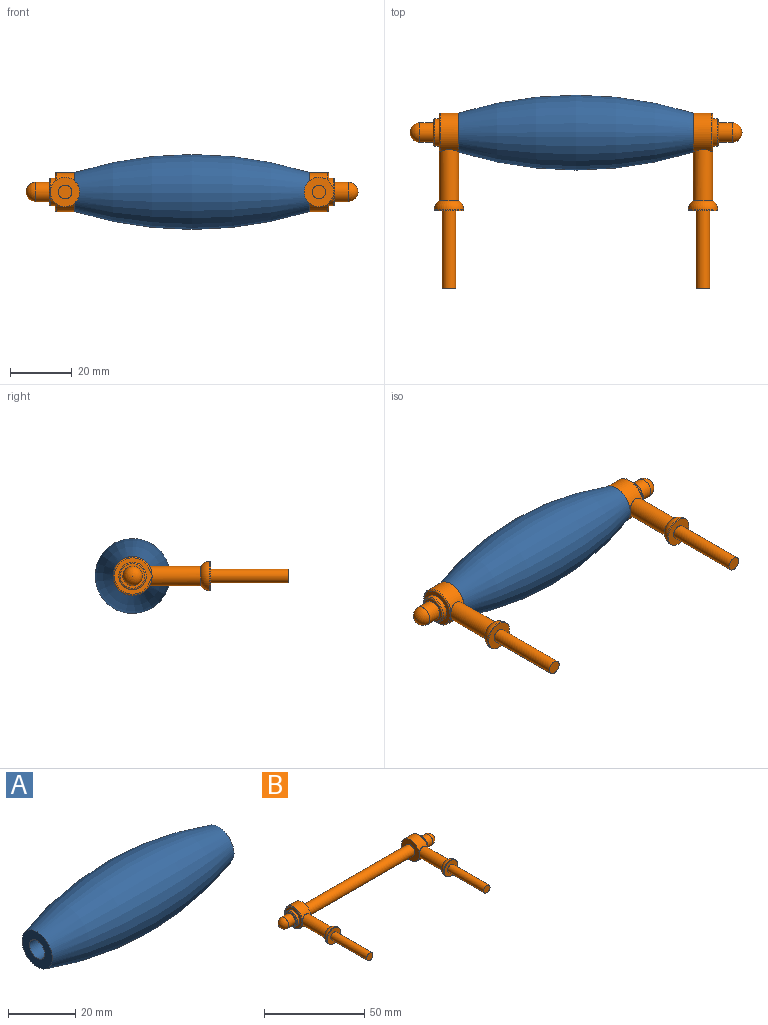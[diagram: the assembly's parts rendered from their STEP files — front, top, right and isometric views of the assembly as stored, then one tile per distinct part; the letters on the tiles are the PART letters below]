
ASSEMBLY  parts=2 mates=1
PART A: 4 faces, bbox 76.2x24.4x24.4 mm
  f0: cylinder r=3.17mm len=76.2mm, axis (-1,0,0), area 1520.1mm2, adj f1,f3
  f1: plane 12.7x12.7mm, normal (1,0,0), area 95mm2, adj f0,f2
  f2: revolved ~76.2x24.4mm, area 4981.2mm2, adj f1,f3
  f3: plane 12.7x12.7mm, normal (-1,0,0), area 95mm2, adj f0,f2
PART B: 35 faces, bbox 108x57.7x13.8 mm
  f0: cylinder r=3.17mm len=16.09mm, axis (0,1,0), area 318.8mm2, adj f2,f26,f28,f34
  f1: cylinder r=3.17mm len=16.09mm, axis (0,1,0), area 318.8mm2, adj f3,f29,f31,f33
  f2: cylinder r=6.35mm len=12.7mm, axis (-1,0,0), area 203.8mm2, adj f0,f7,f27
  f3: cylinder r=6.35mm len=12.7mm, axis (-1,0,0), area 203.8mm2, adj f1,f9,f30
  f4: plane 8x8mm, normal (1,0,0), area 18.6mm2, adj f16,f25
  f5: cylinder r=4.45mm len=8.89mm, axis (-1,0,0), area 40.8mm2, adj f6,f25
  f6: plane 12.26x11.81mm, normal (1,0,0), area 48mm2, adj f5,f26,f27,f28
  f7: plane 12.7x12.7mm, normal (-1,0,0), area 95mm2, adj f2,f8
  f8: cylinder r=3.17mm len=76.2mm, axis (-1,0,0), area 1520.1mm2, adj f7,f9
  f9: plane 12.7x12.7mm, normal (1,0,0), area 95mm2, adj f3,f8
  f10: plane 12.26x11.81mm, normal (-1,0,0), area 48mm2, adj f11,f29,f30,f31
  f11: cylinder r=4.45mm len=8.89mm, axis (-1,0,0), area 40.8mm2, adj f10,f32
  f12: plane 8x8mm, normal (-1,0,0), area 18.6mm2, adj f13,f32
  f13: cylinder r=3.17mm len=6.35mm, axis (-1,0,0), area 88.7mm2, adj f12,f14
  f14: sphere r=3.17mm, area 63.3mm2, adj f13
  f15: sphere r=3.17mm, area 63.3mm2, adj f16
  f16: cylinder r=3.17mm len=6.35mm, axis (-1,0,0), area 88.7mm2, adj f4,f15
  f17: cylinder r=4.76mm len=9.53mm, axis (0,-1,0), area 12.7mm2, adj f20,f33
  f18: plane 4.45x4.45mm, normal (0,-1,0), area 15.5mm2, adj f19
  f19: cylinder r=2.22mm len=25.4mm, axis (0,1,0), area 354.7mm2, adj f18,f20
  f20: plane 9.53x9.53mm, normal (0,-1,0), area 55.7mm2, adj f17,f19
  f21: cylinder r=4.76mm len=9.53mm, axis (0,-1,0), area 12.7mm2, adj f24,f34
  f22: plane 4.45x4.45mm, normal (0,-1,0), area 15.5mm2, adj f23
  f23: cylinder r=2.22mm len=25.4mm, axis (0,1,0), area 354.7mm2, adj f22,f24
  f24: plane 9.53x9.53mm, normal (0,-1,0), area 55.7mm2, adj f21,f23
  f25: torus R=4mm, axis (1,0,0), area 18.8mm2, adj f4,f5
  f26: bspline ~1.72x0.67mm, area 0.4mm2, adj f0,f6,f27
  f27: torus R=5.91mm, axis (1,0,0), area 24.9mm2, adj f2,f6,f26,f28
  f28: bspline ~1.84x0.69mm, area 0.4mm2, adj f0,f6,f27
  f29: bspline ~1.84x0.69mm, area 0.4mm2, adj f1,f10,f30
  f30: torus R=5.91mm, axis (1,0,0), area 24.9mm2, adj f3,f10,f29,f31
  f31: bspline ~1.72x0.67mm, area 0.4mm2, adj f1,f10,f30
  f32: torus R=4mm, axis (1,0,0), area 18.8mm2, adj f11,f12
  f33: torus R=1.59mm, axis (0,1,0), area 88mm2, adj f1,f17
  f34: torus R=1.59mm, axis (0,1,0), area 88mm2, adj f0,f21
PLACE A t=(21.78,20.34,11.64)mm
PLACE B t=(21.78,20.34,11.64)mm
MATE fastened B.f2 <-> A.f0  axis (1,0,0) through (-16.32,20.34,11.64)mm
